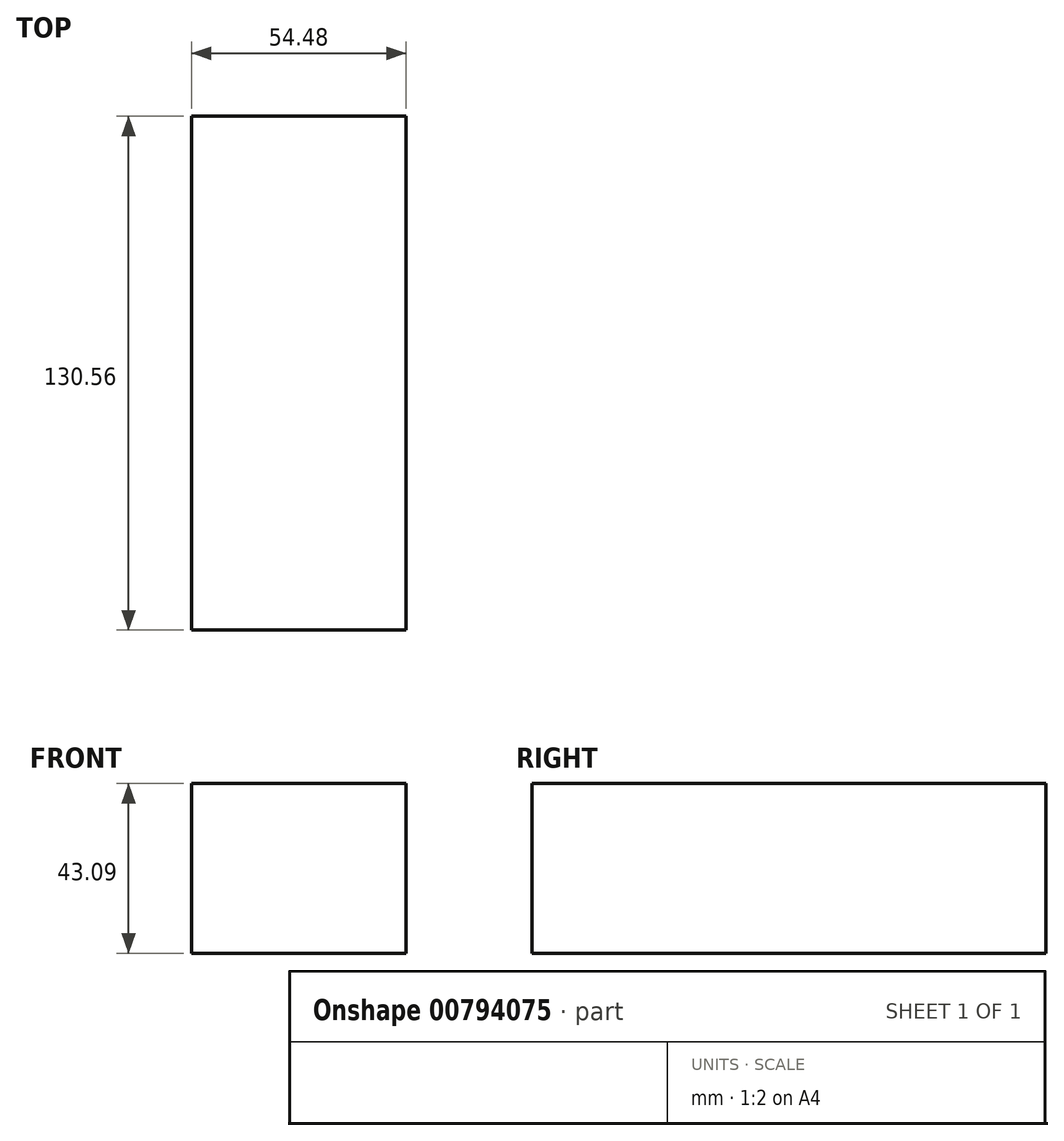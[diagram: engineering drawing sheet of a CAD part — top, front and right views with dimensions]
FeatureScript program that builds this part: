
annotation { "Feature Type Name" : "Feature", "Feature Type Description" : "" }
export const myFeature = defineFeature(function(context is Context, id is Id, definition is map)
    precondition{}
    {
        {
            var Q0;
            Q0=qCreatedBy(makeId("Front.planeOp"),FACE);
            var sketch = newSketch(context, id + "F0", { "sketchPlane" : qUnion([Q0])});
            skLineSegment(sketch, "E0.bottom", {"start": v(0, 0) * mm, "end": v(54.48, 0) * mm});
            skLineSegment(sketch, "E0.top", {"start": v(0, 43.1) * mm, "end": v(54.48, 43.1) * mm});
            skLineSegment(sketch, "E0.left", {"start": v(0, 0) * mm, "end": v(0, 43.1) * mm});
            skLineSegment(sketch, "E0.right", {"start": v(54.48, 0) * mm, "end": v(54.48, 43.1) * mm});
            skSolve(sketch);
        }
        {
            var Q0;
            Q0 = qSketchRegion(id + "F0", true);
            extrude(context, id + "F1", {"entities" : qUnion([Q0]), "depth" : 130.56 * mm, "offsetDistance" : 25.4 * mm});
        }
    });
